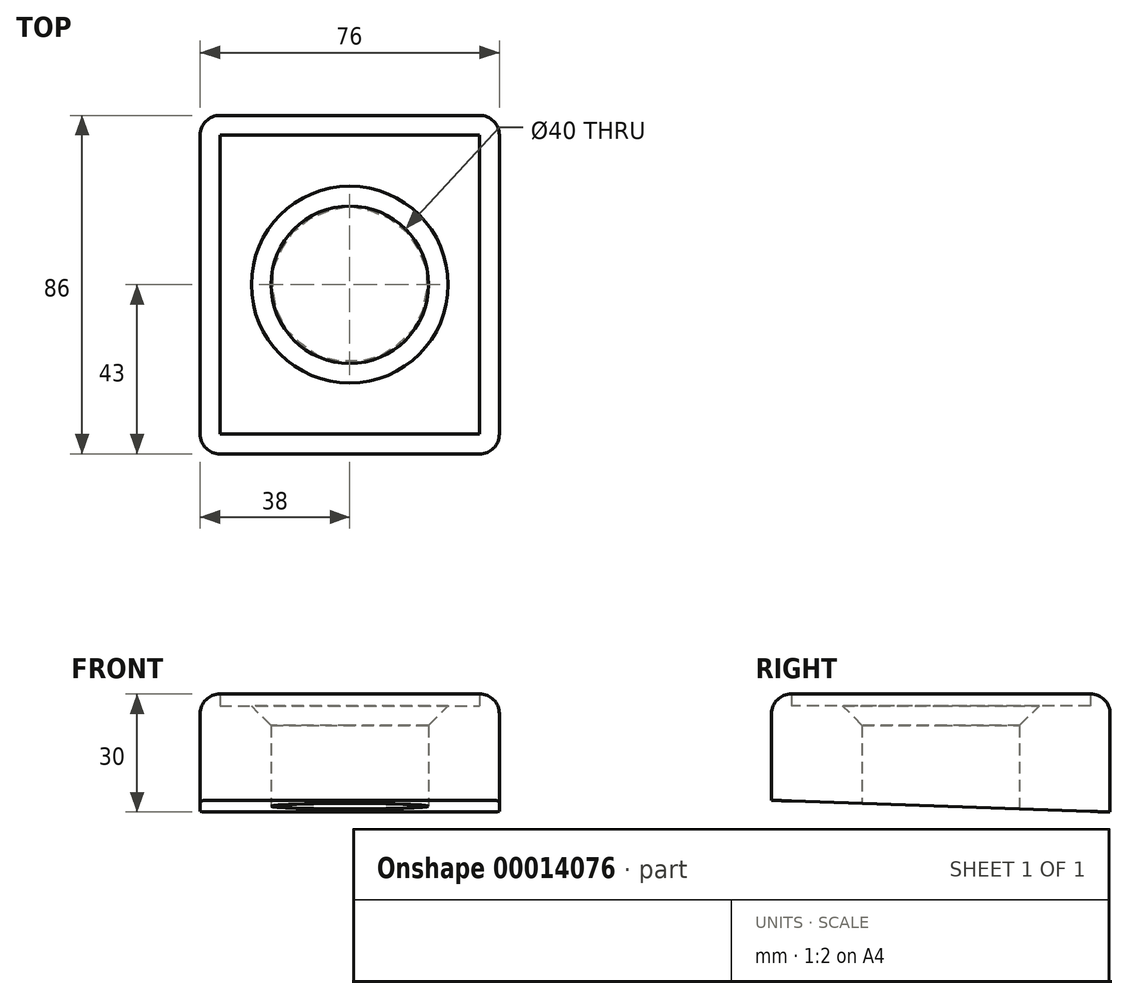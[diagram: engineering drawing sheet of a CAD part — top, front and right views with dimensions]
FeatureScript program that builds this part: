
annotation { "Feature Type Name" : "Feature", "Feature Type Description" : "" }
export const myFeature = defineFeature(function(context is Context, id is Id, definition is map)
    precondition{}
    {
        {
            var Q0;
            Q0=qCreatedBy(makeId("Top.planeOp"),FACE);
            var sketch = newSketch(context, id + "F0", { "sketchPlane" : qUnion([Q0])});
            skLineSegment(sketch, "E0.bottom", {"start": v(0, 0) * mm, "end": v(66, 0) * mm});
            skLineSegment(sketch, "E0.top", {"start": v(0, -76) * mm, "end": v(66, -76) * mm});
            skLineSegment(sketch, "E0.left", {"start": v(0, 0) * mm, "end": v(0, -76) * mm});
            skLineSegment(sketch, "E0.right", {"start": v(66, 0) * mm, "end": v(66, -76) * mm});
            skLineSegment(sketch, "E1", {"start": v(0, 0) * mm, "end": v(66, -76) * mm});
            skCircle(sketch, "E2", {"center": v(33, -38) * mm, "radius": 20 * mm});
            skLineSegment(sketch, "E3.rect.bottom", {"start": v(71, -81) * mm, "end": v(-5, -81) * mm});
            skLineSegment(sketch, "E3.rect.top", {"start": v(71, 5) * mm, "end": v(-5, 5) * mm});
            skLineSegment(sketch, "E3.rect.left", {"start": v(71, -81) * mm, "end": v(71, 5) * mm});
            skLineSegment(sketch, "E3.rect.right", {"start": v(-5, -81) * mm, "end": v(-5, 5) * mm});
            skSolve(sketch);
        }
        {
            var Q0;
            {var subQ5=sQuery(id+"F0.wireOp",EDGE,"E0.bottom");Q0=makeQuery(id+"F0.imprint","IMPRINT",FACE,{"disambiguationData":[TD([[makeQuery(id+"F0.imprint","IMPRINT",EDGE,{"derivedFrom":subQ5}),-1.0]])]});}
            var Q1;
            {var subQ4=sQuery(id+"F0.wireOp",EDGE,"E0.top");Q1=makeQuery(id+"F0.imprint","IMPRINT",FACE,{"disambiguationData":[TD([[makeQuery(id+"F0.imprint","IMPRINT",EDGE,{"derivedFrom":subQ4}),1.0]])]});}
            extrude(context, id + "F1", {"entities" : qUnion([Q0, Q1]), "depth" : 24 * mm});
        }
        {
            var Q0;
            Q0=makeQuery(id+"F0.imprint","IMPRINT",FACE,{"disambiguationData":[TD([[makeQuery(id+"F0.imprint","IMPRINT",EDGE,{"derivedFrom":sQuery(id+"F0.wireOp",EDGE,"E0.bottom")}),1.0]])]});
            extrude(context, id + "F2", {"entities" : qUnion([Q0]), "operationType" : NewBodyOperationType.ADD, "depth" : 27 * mm});
        }
        {
            var Q0;
            Q0=makeQuery(id+"F2.opExtrude","CAP_EDGE",EDGE,{"disambiguationData":[OSD([sQuery(id+"F0.wireOp",EDGE,"E3.rect.bottom")])],"isStart":false});
            fillet(context, id + "F3", {"entities" : qUnion([Q0]), "radius" : 5 * mm, "tangentPropagation" : true, "allowEdgeOverflow" : false});
        }
        {
            var Q0;
            Q0=makeQuery(id+"F1.opExtrude","CAP_EDGE",EDGE,{"disambiguationData":[OSD([sQuery(id+"F0.wireOp",EDGE,"E2")])],"isStart":false});
            chamfer(context, id + "F4", {"entities" : qUnion([Q0]), "width" : 5 * mm, "tangentPropagation" : true});
        }
        {
            var Q0;
            Q0=makeQuery(id+"F0.imprint","IMPRINT",FACE,{"disambiguationData":[TD([[makeQuery(id+"F0.imprint","IMPRINT",EDGE,{"derivedFrom":sQuery(id+"F0.wireOp",EDGE,"E0.bottom")}),1.0]])]});
            extrude(context, id + "F5", {"entities" : qUnion([Q0]), "operationType" : NewBodyOperationType.ADD, "oppositeDirection" : true, "depth" : 3 * mm});
        }
        {
            var Q0;
            {var subQ4=sQuery(id+"F0.wireOp",EDGE,"E0.top");Q0=makeQuery(id+"F0.imprint","IMPRINT",FACE,{"disambiguationData":[TD([[makeQuery(id+"F0.imprint","IMPRINT",EDGE,{"derivedFrom":subQ4}),1.0]])]});}
            var Q1;
            {var subQ5=sQuery(id+"F0.wireOp",EDGE,"E0.bottom");Q1=makeQuery(id+"F0.imprint","IMPRINT",FACE,{"disambiguationData":[TD([[makeQuery(id+"F0.imprint","IMPRINT",EDGE,{"derivedFrom":subQ5}),-1.0]])]});}
            extrude(context, id + "F6", {"entities" : qUnion([Q0, Q1]), "operationType" : NewBodyOperationType.ADD, "oppositeDirection" : true, "depth" : 3 * mm});
        }
        {
            var Q0;
            {var subQ0=sQuery(id+"F0.wireOp",EDGE,"E3.rect.right");Q0=makeQuery(id+"F5.boolean.opBoolean","MERGE",FACE,{"derivedFrom":[makeQuery(id+"F2.opExtrude","SWEPT_FACE",FACE,{"disambiguationData":[OSD([subQ0])]}),makeQuery(id+"F5.opExtrude","SWEPT_FACE",FACE,{"disambiguationData":[OSD([subQ0])]})]});}
            var sketch = newSketch(context, id + "F7", { "sketchPlane" : qUnion([Q0])});
            skLineSegment(sketch, "E4", {"start": v(-5, -3) * mm, "end": v(81, 0) * mm});
            skSolve(sketch);
        }
        {
            var Q0;
            Q0=makeQuery(id+"F7.imprint","IMPRINT",FACE,{"disambiguationData":[TD([[makeQuery(id+"F7.imprint","IMPRINT",EDGE,{"derivedFrom":sQuery(id+"F7.wireOp",EDGE,"E4")}),-1.0]])]});
            extrude(context, id + "F8", {"entities" : qUnion([Q0]), "operationType" : NewBodyOperationType.REMOVE, "oppositeDirection" : true, "depth" : 78.96 * mm});
        }
        {
            var Q0;
            {var subQ0=sQuery(id+"F0.wireOp",EDGE,"E3.rect.top");var subQ1=sQuery(id+"F0.wireOp",EDGE,"E3.rect.left");Q0=makeQuery(id+"F5.boolean.opBoolean","MERGE",EDGE,{"derivedFrom":[makeQuery(id+"F2.opExtrude","SWEPT_EDGE",EDGE,{"disambiguationData":[OSD([subQ0,subQ1])]}),makeQuery(id+"F5.opExtrude","SWEPT_EDGE",EDGE,{"disambiguationData":[OSD([subQ0,subQ1])]})]});}
            fillet(context, id + "F9", {"entities" : qUnion([Q0]), "radius" : 5 * mm, "tangentPropagation" : true, "allowEdgeOverflow" : false});
        }
        {
            var Q0;
            {var subQ0=sQuery(id+"F0.wireOp",EDGE,"E3.rect.top");var subQ1=sQuery(id+"F0.wireOp",EDGE,"E3.rect.right");Q0=makeQuery(id+"F5.boolean.opBoolean","MERGE",EDGE,{"derivedFrom":[makeQuery(id+"F2.opExtrude","SWEPT_EDGE",EDGE,{"disambiguationData":[OSD([subQ0,subQ1])]}),makeQuery(id+"F5.opExtrude","SWEPT_EDGE",EDGE,{"disambiguationData":[OSD([subQ0,subQ1])]})]});}
            fillet(context, id + "F10", {"entities" : qUnion([Q0]), "radius" : 5 * mm, "tangentPropagation" : true, "allowEdgeOverflow" : false});
        }
        {
            var Q0;
            {var subQ0=sQuery(id+"F0.wireOp",EDGE,"E3.rect.bottom");var subQ1=sQuery(id+"F0.wireOp",EDGE,"E3.rect.left");Q0=makeQuery(id+"F5.boolean.opBoolean","MERGE",EDGE,{"derivedFrom":[makeQuery(id+"F2.opExtrude","SWEPT_EDGE",EDGE,{"disambiguationData":[OSD([subQ0,subQ1])]}),makeQuery(id+"F5.opExtrude","SWEPT_EDGE",EDGE,{"disambiguationData":[OSD([subQ0,subQ1])]})]});}
            fillet(context, id + "F11", {"entities" : qUnion([Q0]), "radius" : 5 * mm, "tangentPropagation" : true, "allowEdgeOverflow" : false});
        }
    });
